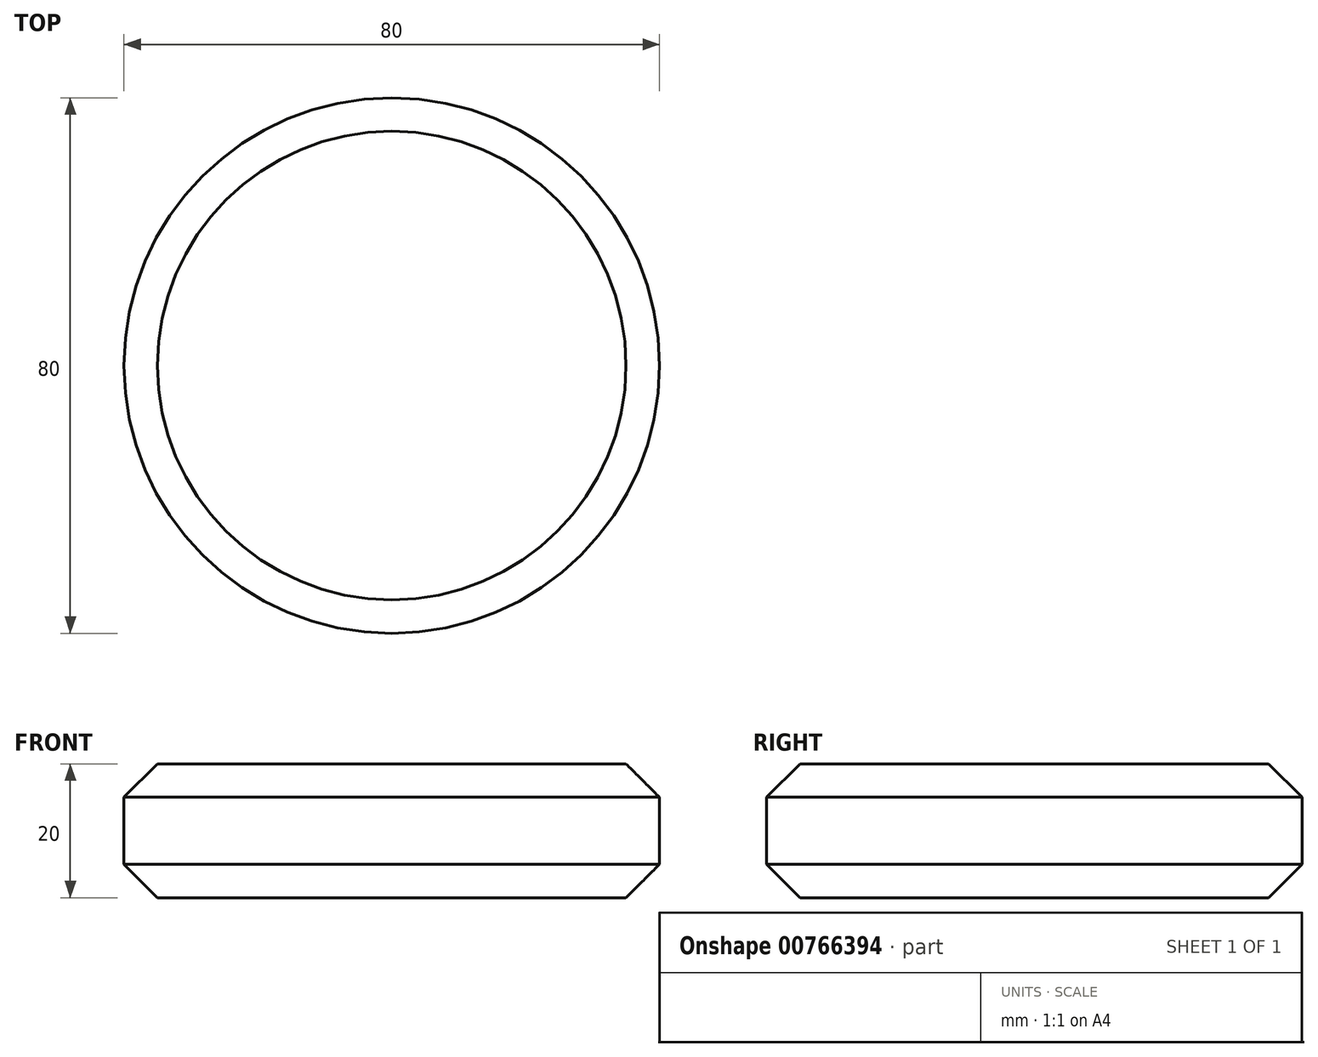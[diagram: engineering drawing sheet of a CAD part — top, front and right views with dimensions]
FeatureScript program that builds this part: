
annotation { "Feature Type Name" : "Feature", "Feature Type Description" : "" }
export const myFeature = defineFeature(function(context is Context, id is Id, definition is map)
    precondition{}
    {
        {
            assignVariable(context, id + "F0", {"name" : "MainDiscHeight", "anyValue" : 20});
        }
        {
            assignVariable(context, id + "F1", {"name" : "StandardChamfer", "anyValue" : 5});
        }
        {
            var Q0;
            Q0=qCreatedBy(makeId("Top.planeOp"),FACE);
            var sketch = newSketch(context, id + "F2", { "sketchPlane" : qUnion([Q0])});
            skCircle(sketch, "E0", {"center": v(0, 0) * mm, "radius": 40 * mm});
            skSolve(sketch);
        }
        {
            var Q0;
            Q0 = qSketchRegion(id + "F2", true);
            extrude(context, id + "F3", {"entities" : qUnion([Q0]), "depth" : (getVariable(context, 'MainDiscHeight')) * mm, "offsetDistance" : 25 * mm});
        }
        {
            var Q0;
            Q0=makeQuery(id+"F3.opExtrude","CAP_EDGE",EDGE,{"disambiguationData":[OSD([sQuery(id+"F2.wireOp",EDGE,"E0")])],"isStart":false});
            chamfer(context, id + "F4", {"entities" : qUnion([Q0]), "width" : (getVariable(context, 'StandardChamfer')) * mm, "tangentPropagation" : true});
        }
        {
            var Q0;
            Q0=makeQuery(id+"F3.opExtrude","CAP_EDGE",EDGE,{"disambiguationData":[OSD([sQuery(id+"F2.wireOp",EDGE,"E0")])],"isStart":true});
            chamfer(context, id + "F5", {"entities" : qUnion([Q0]), "width" : (getVariable(context, 'StandardChamfer')) * mm, "tangentPropagation" : true});
        }
    });
